# Revit family: 759405_V
name_source: partatom
category: Luminaires
units: mm (PartAtom-declared; Revit-internal decimal feet)

## family parameters
Cote de connecteur circulaire = Utiliser le diamètre
Couper avec des vides une fois chargée = Oui
Hôte = Face
Numéro OmniClass = 23.80.70.11.14.11
Partagée = Oui
Point de calcul de pièce = Oui
Source d'éclairage = Oui
Titre OmniClass = Downlights
Type d'élément = Normal

## types (2) — shared parameters
Angle de l'inclinaison = 60.00°
Charge apparente = 20 VA
Commentaires relatifs à la puissance = 18.9W
Description = Downlight équipé d'un module LED SMD, efficacité lumineuse de 116lm/W
Diamètre = 220 mm  [stored 0.721785 ft]
Diamètre collerette = 171 mm  [stored 0.561024 ft]
Emettre la visibilité des formes dans le rendu = Non
Emettre à partir du diamètre du cercle = 610 mm
Fabricant = Résistex
Filtre de couleur = 16777215
Garantie = 2 ans
Gradation des changements de température de couleur de lampe = <Aucun>
IK = 07
IP = 20
Image du type = <Aucun>
Indice de charge = Eclairage
Matériau corps = PC Blanc
Matériau diffuseur = PC Transparent
Modèle = Muse
Nombre pôles = 1
Tension = 230 V
URL = https://www.resistex-sa.com
Épaisseur = 18 mm  [stored 0.0590551 ft]
Épaisseur diffuseur = 2 mm  [stored 0.00656168 ft]
zero-valued in all types: Elévation par défaut

## per-type parameters (varying)
| type | Coût | Fichier de distribution photométrique |
| 759405 | 35 $ | 759405.ies |
| 759406 | 52.5 $ | 759406.ies |

note: [stored X ft] marks values corroborated as IEEE doubles in the binary element streams (Revit-internal decimal feet)
